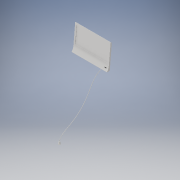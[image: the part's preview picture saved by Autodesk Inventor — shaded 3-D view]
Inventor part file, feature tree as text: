
AUTODESK INVENTOR PART (.ipt)
format: ipt  version: 2017 (Build 210142000, 142)  size: 406,528 bytes
history: native  units: in
note: dims shown in document units (in); Inventor stores cm internally (conversion verified against a paired STEP export)
features: sketch x12, extrude x9, other x5, plane x2, sweep x1, loft x1
ambient origin geometry x8: Origin, YZ Plane, XZ Plane, XY Plane, X Axis, Y Axis, Z Axis, Center Point
bodies: Solid1 (feature_tree), Solid2 (feature_tree), Solid3 (feature_tree)
feature tree (30):
  extrude  "block to cut from"  Depth=1.7188in
  extrude  "side view correct"  Depth=0.0104in
  extrude  "top view correct"  Depth=0.5841in
  plane  "Work Plane1"
  extrude  "slight top view correction"  Depth=0.0104in
  extrude  "screen"  TaperAngle=135.0deg  [1 undecoded]
  plane  "Work Plane2"
  extrude  "light cutout"  Depth=0.9583in
  sketch  "Sketch8"  dims[d17=0.0729in d19=0.1807in]
  extrude  "power indicator"  Depth=0.1807in
  extrude  "power button"  Depth=0.4271in TaperAngle=0.0deg
  extrude  "power symble"  Depth=0.3333in
  sweep  "Sweep1"
  sketch  "Sketch14"  dims[d25=0.4271in d26=0.0in d27=90.0deg]
  other  "plug bottom workplane"
  loft  "Loft1"
  other  "mate plane middle"
  other  "mate to back of stand"
  sketch  "Sketch1"  dims[d0=1.1771in d1=1.7188in]
  sketch  "Sketch2"  dims[d2=0.5527in d3=0.0in d4=0.0104in]
  sketch  "Sketch3"  dims[d6=0.3125in d7=0.5841in]
  sketch  "Sketch4"  dims[d8=0.6927in d12=0.0104in]
  sketch  "Sketch5"  dims[d13=0.0677in d14=135.0deg]
  sketch  "Sketch7"  dims[d15=0.1042in d16=0.9583in]
  sketch  "Sketch11"  dims[d20=5.6652in d21=0.4271in d22=0.0in]
  other  "cord line"
  sketch  "Sketch13"  dims[d23=0.3333in d24=0.3333in]
  other  "plug middle workplane"
  sketch  "Sketch15"  dims[d28=0.0625in d29=1.4896in d30=0.0in]
  sketch  "Sketch16"  dims[d32=0.0781in d33=0.0833in d34=0.0781in d35=0.0833in d36=0.0208in d37=0.0in d38=0.0625in d40=45.0deg d49=0.0938in d50=0.0762in d51=0.021in d52=0.03in d53=0.0in d54=0.0749in d55=0.0013in d56=0.0185in d57=0.03in d58=0.0in d59=0.017in d60=0.0137in d61=0.0in d73=0.0019in d76=0.001in d77=0.001in d78=0.001in d79=0.0in d81=0.3827in d82=0.3937in d83=0.02in d84=0.3827in d85=0.0in d86=0.0in d87=0.0366in d88=0.0535in d89=0.0837in d90=0.0535in d91=0.0829in d92=0.0454in d93=0.0364in d94=0.0364in d95=0.0105in d96=0.0052in d97=0.0453in d98=0.0329in d99=0.0in d100=90.0deg d101=0.0in d102=90.0deg d103=0.0in d104=90.0deg]
note: 1 required parameter value undecoded (feature->parameter linkage not recoverable at this tier; creation-order binding heuristic only, values carry confidence <= 0.55)
